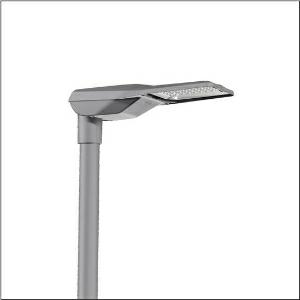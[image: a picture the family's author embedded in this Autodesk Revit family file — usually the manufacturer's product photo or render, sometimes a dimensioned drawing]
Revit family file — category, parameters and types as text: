
# Revit family: streetlight_sl_21_iq_mini___st1_0a_5xe2d31g08hb_3bda
name_source: partatom
category: Lighting Fixtures
units: mm (PartAtom-declared; Revit-internal decimal feet)

## family parameters
Cut with Voids When Loaded = No
Host = Face
Light Source = No
Part Type = Normal
Room Calculation Point = No
Round Connector Dimension = Use Diameter
Shared = No

## types (1)
- --- (1 x LED, 9450 lm, 70.9 W, 3000K)
    Apparent Load = 71 VA
    CIE Flux Codes = 37 72 97 100 100
    Color Rendering = 70
    Color Temperature = 3000K
    Default Elevation = 1800 mm
    Description = Streetlight SL 21 iQ mini, mast luminaire, primary light control with lens, of PMMA, primary optical cover: cover, of toughened safety glass, transparent, light distribution: ST1.0a, light emission: direct distribution, primary light characteristic: asymmetric, installation type: post-top, side-entry, LED, High Power LED, rated luminous flux: 9.450lm, luminous efficacy: 133lm/W, light colour: 730, colour temperature: 3000K, control gear: iQ Street-Remote, control: Street-Remote, Auto-Match, Temp-Guard, Lumen-Switch, Night-Set, Smart-Wire, Light-Fading, Desk-Remote (wireless, voltage-free reading and setting of iQ features in the workshop via application-optimized NFC function/RFID function), optimised constant luminous flux control (CLO 2.0), pre-setting: linear dimming characteristic, mains connection: 220..240V, AC, 50/60Hz, start of lifetime: 71W, end of service life: 75W, reduction: 31W, luminaire housing, of diecast aluminium, powder-coated, SITECO metallic grey (DB 702S), corrosivity category C5 high according to DIN EN ISO 12944, please order mast flange separately, inclination adjustable: 0°, 5°, 10°, 15°, sealing non-destructively replaceable, multi-level sealing system, length: 628mm, width: 235mm, height: 110mm, mast flange for spigot size: 42mm (side-entry): 5XC10008XM4, 60/48mm (side-entry/post-top): 5XC10108XM2, 76/60mm (side-entry/post-top): 5XC10108XM1, mounting height: 4..8m, protection rating (complete): IP66, insulation class (complete): insulation class II (safety insulation), certification: CE, ENEC, ENEC+, VDE, impact resistance: IK10, permissible operating ambient temperature for outdoor applications: -40..+50°C, standard-compliant lighting for roads and squares, packaging unit: 1 piece

Light Distribution: ST1.0a
    Height = 110 mm
    Lamp = 1 x LED
    Lamp Light Flux = 9450 lm
    Lamp Power = 70.9 W
    Lamp count = 1
    Length = 625 mm
    Luminous efficacy = 133 lm/W
    Manufacturer = Siteco
    ModVariant = No
    Model = 5XE2D31G08HB
    Number of Poles = 1
    OnlyDefault = Yes
    Power Factor = 1
    Product Name = Streetlight SL 21 iQ mini | ST1.0a
    Product group = mast luminaire | pylon top
    ProductGroupID = 6100
    Protection Class = Protection class II
    Protection Degree = IP 66
    RLX_Detail_Level = 1
    RLX_Emergency_Light_Flux = 0 lm
    RLX_Emergency_Type = 0
    RLX_Emergency_Type_DB = No
    RlxData = <blob elided: 26365 chars, md5=7b8a610d>
    Socket = socket
    Standby Power = 0 W
    System Light Flux = 9450 lm
    System Power = 71 W
    Type Comments = factory setting: luminous flux: 100 % | dim-lin: 254 | 711 mA
    Type Image = l_1003519.jpg
    URL = http://relux.com
    VarID = @adj_157603
    Voltage = 0 V
    Weight = 0.00 kg
    Width = 234 mm

## geometry (parser evidence)
native form markers: Blend x4, Sweep x11
no freeform markers — native parametric forms only
